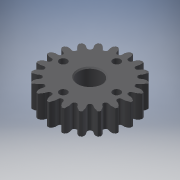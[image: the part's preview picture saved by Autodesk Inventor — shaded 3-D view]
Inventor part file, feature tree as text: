
AUTODESK INVENTOR PART (.ipt)
format: ipt  version: 2016 (Build 200138000, 138)  size: 656,896 bytes
history: native  units: mm
features: other x14, sketch x4, revolve x3, extrude x2, hole x1
ambient origin geometry x8: Origin, YZ Plane, XZ Plane, XY Plane, X Axis, Y Axis, Z Axis, Center Point
bodies: Solid1 (feature_tree)
feature tree (24):
  revolve  "Revolution1"  [1 undecoded]
  extrude  "Extrusion1"  TaperAngle=360.0deg  [1 undecoded]
  hole  "Hole1"  [1 undecoded]
  revolve  "Revolution2"  [1 undecoded]
  revolve  "Revolution3"  [1 undecoded]
  other  "b_XY"
  other  "b_YZ"
  other  "b_ZX"
  other  "b_X"
  other  "b_Y"
  other  "b_Z"
  other  "b_Center"
  other  "turn_around_XY"
  other  "turn_around_YZ"
  other  "turn_around_ZX"
  other  "turn_around_X"
  other  "turn_around_Y"
  other  "turn_around_Z"
  other  "turn_around_Center"
  extrude  "押し出し2"  Depth=6.0mm TaperAngle=360.0deg
  sketch  "Sketch_12"  dims[d11=360.0deg d12=0.0mm d13=7.0mm d14=2.0mm d15=40.0mm d17=360.0deg d19=6.0mm d20=0.0mm]
  sketch  "Sketch_3"  dims[d0=360.0deg d1=6.0mm d2=0.0mm]
  sketch  "Sketch3"  dims[d3=6.0mm d4=6.0mm d5=4.0mm d6=2.0mm d7=90.0deg d8=6.0mm d9=0.0mm d10=360.0deg]
  sketch  "スケッチ6"
note: 5 required parameter values undecoded (feature->parameter linkage not recoverable at this tier; creation-order binding heuristic only, values carry confidence <= 0.55)